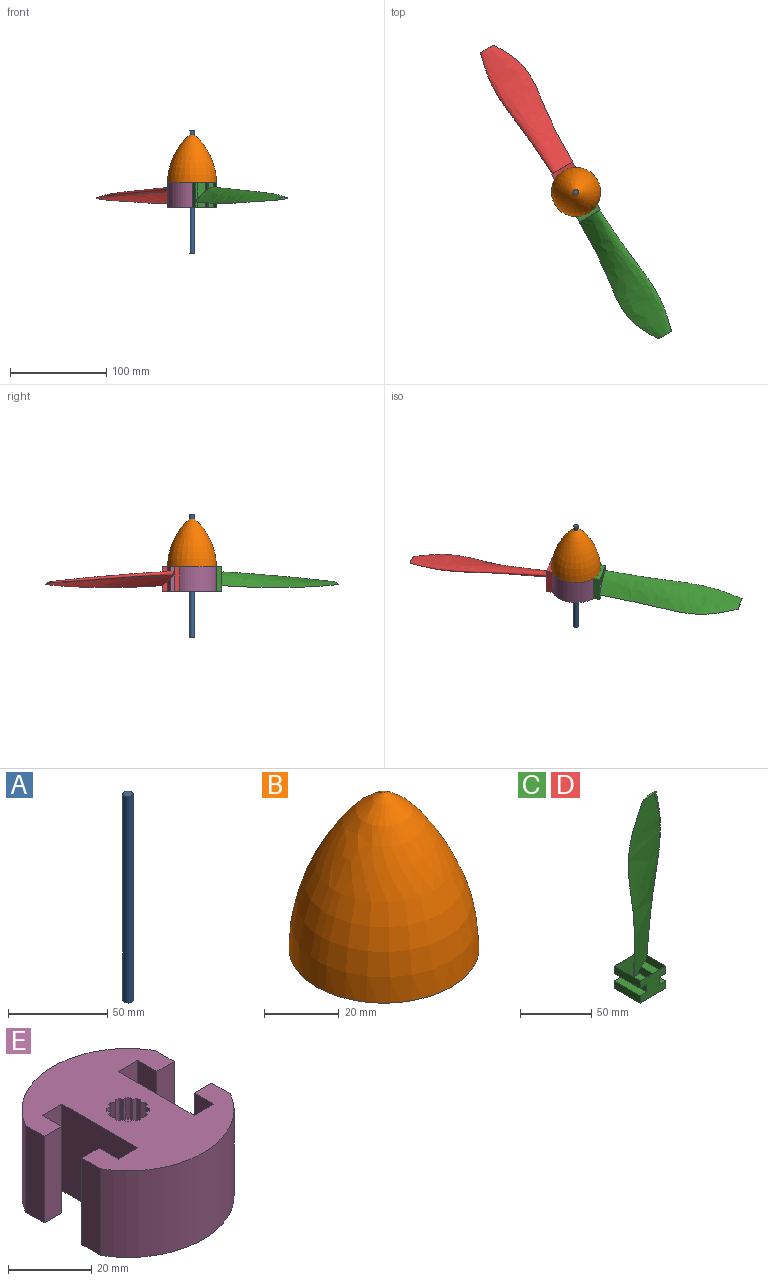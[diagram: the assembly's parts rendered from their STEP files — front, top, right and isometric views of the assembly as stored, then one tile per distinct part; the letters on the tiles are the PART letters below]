
ASSEMBLY  parts=5 mates=4
PART A: 3 faces, bbox 5.1x5.1x127 mm
  f0: cylinder r=2.54mm len=127mm, axis (0,0,-1), area 2026.8mm2, adj f1,f2
  f1: plane 5.08x5.08mm, normal (0,0,1), area 20.3mm2, adj f0
  f2: plane 5.08x5.08mm, normal (0,0,-1), area 20.3mm2, adj f0
PART B: 2 faces, bbox 50.8x50.8x50.8 mm
  f0: plane 50.8x50.8mm, normal (0,0,-1), area 2026.8mm2, adj f1
  f1: revolved ~50.8x50.8mm, area 6238.6mm2, adj f0
PART C: 17 faces, bbox 48.7x25.4x165.1 mm
  f0: plane 25.45x25.45mm, normal (0,0,1), area 541.4mm2, adj f3,f5,f11,f12,f15,f16
  f1: plane 25.4x6.35mm, normal (0,0,1), area 161.3mm2, adj f2,f3,f5,f8
  f2: plane 25.4x6.35mm, normal (1,0,0), area 161.3mm2, adj f1,f3,f5,f7
  f3: plane 25.4x19.05mm, normal (0,1,0), area 403.2mm2, adj f0,f1,f2,f4,f6,f7,f8,f9
  f4: plane 25.4x6.35mm, normal (-1,0,0), area 161.3mm2, adj f3,f5,f6,f7
  f5: plane 25.4x19.05mm, normal (0,-1,0), area 403.2mm2, adj f0,f1,f2,f4,f6,f7,f8,f9
  f6: plane 25.4x6.35mm, normal (0,0,1), area 161.3mm2, adj f3,f4,f5,f9
  f7: plane 25.4x25.4mm, normal (0,0,-1), area 645.2mm2, adj f2,f3,f4,f5
  f8: plane 25.4x6.35mm, normal (1,0,0), area 161.3mm2, adj f1,f3,f5,f13
  f9: plane 25.4x6.35mm, normal (-1,0,0), area 161.3mm2, adj f3,f5,f6,f10
  f10: plane 25.4x6.35mm, normal (0,0,-1), area 161.3mm2, adj f3,f5,f9,f12
  f11: plane 25.4x6.35mm, normal (1,0,0), area 161.3mm2, adj f0,f3,f5,f13
  f12: plane 25.4x6.35mm, normal (-1,0,0), area 161.3mm2, adj f0,f3,f5,f10
  f13: plane 25.4x6.35mm, normal (0,0,-1), area 161.3mm2, adj f3,f5,f8,f11
  f14: plane 15.77x3.2mm, normal (0,0,1), area 21.2mm2, adj f15,f16
  f15: bspline ~146.05x47.36mm, area 4482.7mm2, adj f0,f14,f16
  f16: bspline ~146.05x48.69mm, area 5495.4mm2, adj f0,f14,f15
PART D: same geometry as C
PART E: 60 faces, bbox 44x50.8x25.4 mm
  f0: plane 50.8x43.99mm, normal (0,0,1), area 1348.8mm2, adj f2,f3,f4,f5,f6,f7,f8,f9
  f1: cylinder r=2.79mm len=19.05mm, axis (0,0,1), area 334.4mm2, adj f22,f23
  f2: plane 25.4x6.6mm, normal (0,-1,0), area 167.7mm2, adj f0,f3,f21,f22
  f3: plane 25.4x6.48mm, normal (-1,0,0), area 164.5mm2, adj f0,f2,f4,f22
  f4: plane 25.4x5.84mm, normal (0,-1,0), area 148.4mm2, adj f0,f3,f5,f22
  f5: plane 25.4x6.35mm, normal (1,0,0), area 161.3mm2, adj f0,f4,f6,f22
  f6: cylinder r=25.4mm len=43.99mm, axis (0,0,-1), area 1351.2mm2, adj f0,f5,f7,f22
  f7: plane 25.4x6.35mm, normal (-1,0,0), area 161.3mm2, adj f0,f6,f8,f22
  f8: plane 25.4x5.84mm, normal (0,-1,0), area 148.4mm2, adj f0,f7,f9,f22
  f9: plane 25.4x6.48mm, normal (1,0,0), area 164.5mm2, adj f0,f8,f10,f22
  f10: plane 25.4x6.6mm, normal (0,-1,0), area 167.7mm2, adj f0,f9,f11,f22
  f11: plane 25.65x25.4mm, normal (-1,0,0), area 651.6mm2, adj f0,f10,f12,f22
  f12: plane 25.4x6.6mm, normal (0,1,0), area 167.7mm2, adj f0,f11,f13,f22
  f13: plane 25.4x6.48mm, normal (1,0,0), area 164.5mm2, adj f0,f12,f14,f22
  f14: plane 25.4x5.84mm, normal (0,1,0), area 148.4mm2, adj f0,f13,f15,f22
  f15: plane 25.4x6.35mm, normal (-1,0,0), area 161.3mm2, adj f0,f14,f16,f22
  f16: cylinder r=25.4mm len=43.99mm, axis (0,0,-1), area 1351.2mm2, adj f0,f15,f17,f22
  f17: plane 25.4x6.35mm, normal (1,0,0), area 161.3mm2, adj f0,f16,f18,f22
  f18: plane 25.4x5.84mm, normal (0,1,0), area 148.4mm2, adj f0,f17,f19,f22
  f19: plane 25.4x6.48mm, normal (-1,0,0), area 164.5mm2, adj f0,f18,f20,f22
  f20: plane 25.4x6.6mm, normal (0,1,0), area 167.7mm2, adj f0,f19,f21,f22
  f21: plane 25.65x25.4mm, normal (1,0,0), area 651.6mm2, adj f0,f2,f20,f22
  f22: plane 50.8x43.99mm, normal (0,0,-1), area 1398.2mm2, adj f1,f2,f3,f4,f5,f6,f7,f8
  f23: plane 10.05x10.05mm, normal (0,0,1), area 49.4mm2, adj f1,f24,f25,f26,f27,f28,f29,f30
  f24: plane 6.35x1.01mm, normal (0.22,0.98,0), area 6.6mm2, adj f0,f23,f25,f59
  f25: cylinder r=5.08mm len=6.35mm, axis (0,0,1), area 7.2mm2, adj f0,f23,f24,f26
  f26: plane 6.35x1.01mm, normal (-0.98,-0.22,0), area 6.6mm2, adj f0,f23,f25,f27
  f27: plane 6.35x0.99mm, normal (-0.3,0.96,0), area 6.6mm2, adj f0,f23,f26,f28
  f28: cylinder r=5.08mm len=6.35mm, axis (0,0,1), area 7.2mm2, adj f0,f23,f27,f29
  f29: plane 6.35x0.76mm, normal (-0.73,-0.68,0), area 6.6mm2, adj f0,f23,f28,f30
  f30: plane 6.35x0.76mm, normal (-0.73,0.68,0), area 6.6mm2, adj f0,f23,f29,f31
  f31: cylinder r=5.08mm len=6.35mm, axis (0,0,1), area 7.2mm2, adj f0,f23,f30,f32
  f32: plane 6.35x0.99mm, normal (-0.3,-0.96,0), area 6.6mm2, adj f0,f23,f31,f33
  f33: plane 6.35x1.01mm, normal (-0.98,0.22,0), area 6.6mm2, adj f0,f23,f32,f34
  f34: cylinder r=5.08mm len=6.35mm, axis (0,0,1), area 7.2mm2, adj f0,f23,f33,f35
  f35: plane 6.35x1.01mm, normal (0.22,-0.98,0), area 6.6mm2, adj f0,f23,f34,f36
  f36: plane 6.35x0.99mm, normal (-0.96,-0.3,0), area 6.6mm2, adj f0,f23,f35,f37
  f37: cylinder r=5.08mm len=6.35mm, axis (0,0,1), area 7.2mm2, adj f0,f23,f36,f38
  f38: plane 6.35x0.76mm, normal (0.68,-0.73,0), area 6.6mm2, adj f0,f23,f37,f39
  f39: plane 6.35x0.76mm, normal (-0.68,-0.73,0), area 6.6mm2, adj f0,f23,f38,f40
  f40: cylinder r=5.08mm len=6.35mm, axis (0,0,1), area 7.2mm2, adj f0,f23,f39,f41
  f41: plane 6.35x0.99mm, normal (0.96,-0.3,0), area 6.6mm2, adj f0,f23,f40,f42
  f42: plane 6.35x1.01mm, normal (-0.22,-0.98,0), area 6.6mm2, adj f0,f23,f41,f43
  f43: cylinder r=5.08mm len=6.35mm, axis (0,0,1), area 7.2mm2, adj f0,f23,f42,f44
  f44: plane 6.35x1.01mm, normal (0.98,0.22,0), area 6.6mm2, adj f0,f23,f43,f45
  f45: plane 6.35x0.99mm, normal (0.3,-0.96,0), area 6.6mm2, adj f0,f23,f44,f46
  f46: cylinder r=5.08mm len=6.35mm, axis (0,0,1), area 7.2mm2, adj f0,f23,f45,f47
  f47: plane 6.35x0.76mm, normal (0.73,0.68,0), area 6.6mm2, adj f0,f23,f46,f48
  f48: plane 6.35x0.76mm, normal (0.73,-0.68,0), area 6.6mm2, adj f0,f23,f47,f49
  f49: cylinder r=5.08mm len=6.35mm, axis (0,0,1), area 7.2mm2, adj f0,f23,f48,f50
  f50: plane 6.35x0.99mm, normal (0.3,0.96,0), area 6.6mm2, adj f0,f23,f49,f51
  f51: plane 6.35x1.01mm, normal (0.98,-0.22,0), area 6.6mm2, adj f0,f23,f50,f52
  f52: cylinder r=5.08mm len=6.35mm, axis (0,0,1), area 7.2mm2, adj f0,f23,f51,f53
  f53: plane 6.35x1.01mm, normal (-0.22,0.98,0), area 6.6mm2, adj f0,f23,f52,f54
  f54: plane 6.35x0.99mm, normal (0.96,0.3,0), area 6.6mm2, adj f0,f23,f53,f55
  f55: cylinder r=5.08mm len=6.35mm, axis (0,0,1), area 7.2mm2, adj f0,f23,f54,f56
  f56: plane 6.35x0.76mm, normal (-0.68,0.73,0), area 6.6mm2, adj f0,f23,f55,f57
  f57: plane 6.35x0.76mm, normal (0.68,0.73,0), area 6.6mm2, adj f0,f23,f56,f58
  f58: cylinder r=5.08mm len=6.35mm, axis (0,0,1), area 7.2mm2, adj f0,f23,f57,f59
  f59: plane 6.35x0.99mm, normal (-0.96,0.3,0), area 6.6mm2, adj f0,f23,f24,f58
PLACE A t=(-33.63,-38.59,-128.02)mm fixed
PLACE B rot(axis=(0,0,-1),59.7deg) t=(-33.63,-38.59,-55)mm
PLACE C rot(axis=(0.93,0.25,0.25),93.9deg) t=(-28.81,-46.84,-67.7)mm
PLACE D rot(axis=(0.19,-0.69,-0.69),158.7deg) t=(-38.44,-30.34,-67.7)mm
PLACE E rot(axis=(0.87,-0.5,0),180deg) t=(-33.63,-38.59,-55)mm
MATE fastened D.f7 <-> E.f11  axis (0.5,-0.86,0) through (-38.44,-30.34,-67.7)mm
MATE revolute A.f0 <-> E.f1  axis (0,0,-1) through (-33.63,-38.59,-64.52)mm
MATE fastened C.f7 <-> E.f21  axis (-0.5,0.86,0) through (-28.81,-46.84,-67.7)mm
MATE fastened E.f6 <-> B.f0  axis (0,0,1) through (-33.63,-38.59,-55)mm
